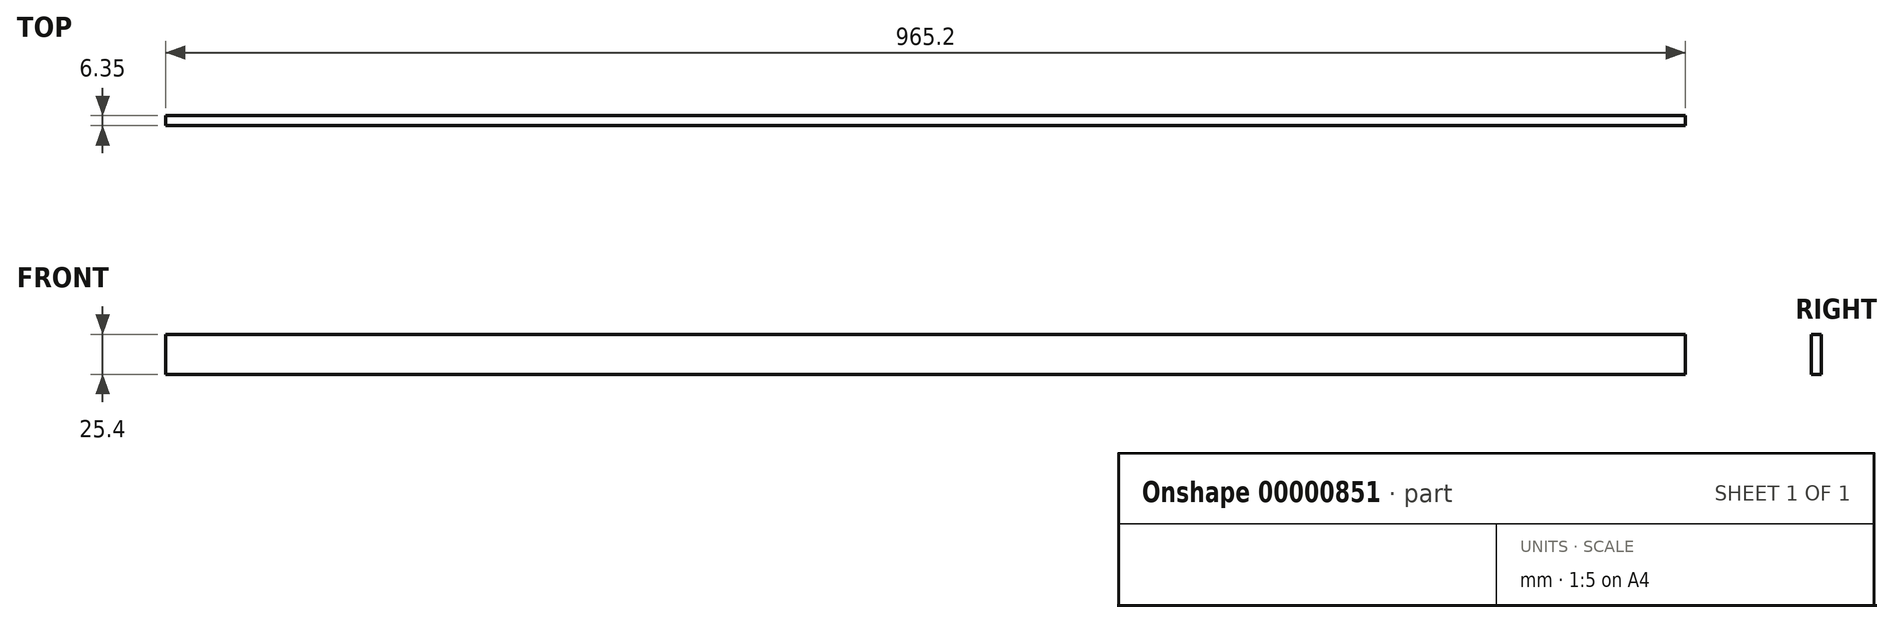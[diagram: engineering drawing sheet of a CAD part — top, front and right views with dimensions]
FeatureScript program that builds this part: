
annotation { "Feature Type Name" : "Feature", "Feature Type Description" : "" }
export const myFeature = defineFeature(function(context is Context, id is Id, definition is map)
    precondition{}
    {
        {
            var Q0;
            Q0=qCreatedBy(makeId("Front.planeOp"),FACE);
            var sketch = newSketch(context, id + "F0", { "sketchPlane" : qUnion([Q0])});
            skLineSegment(sketch, "E0.bottom", {"start": v(-482.6, 25.4) * mm, "end": v(0, 25.4) * mm});
            skLineSegment(sketch, "E0.top", {"start": v(-482.6, 0) * mm, "end": v(0, 0) * mm});
            skLineSegment(sketch, "E0.left", {"start": v(-482.6, 25.4) * mm, "end": v(-482.6, 0) * mm});
            skLineSegment(sketch, "E0.right", {"start": v(0, 25.4) * mm, "end": v(0, 0) * mm});
            skSolve(sketch);
        }
        {
            var Q0;
            Q0=makeQuery(id+"F0.imprint","IMPRINT",FACE,{"disambiguationData":[TD([[makeQuery(id+"F0.imprint","IMPRINT",EDGE,{"derivedFrom":sQuery(id+"F0.wireOp",EDGE,"E0.bottom")}),-1.0]])]});
            extrude(context, id + "F1", {"entities" : qUnion([Q0]), "oppositeDirection" : true, "depth" : 6.35 * mm});
        }
        {
            var Q0;
            Q0=makeQuery(id+"F1.opExtrude","SWEPT_BODY",BODY,{"disambiguationData":[OSD([sQuery(id+"F0.wireOp",EDGE,"E0.bottom"),sQuery(id+"F0.wireOp",EDGE,"E0.top"),sQuery(id+"F0.wireOp",EDGE,"E0.left"),sQuery(id+"F0.wireOp",EDGE,"E0.right")])]});
            var Q1;
            Q1=makeQuery(id+"F1.opExtrude","SWEPT_FACE",FACE,{"disambiguationData":[OSD([sQuery(id+"F0.wireOp",EDGE,"E0.right")])]});
            mirror(context, id + "F2", {"operationType" : NewBodyOperationType.ADD, "entities" : qUnion([Q0]), "mirrorPlane" : qUnion([Q1])});
        }
    });
